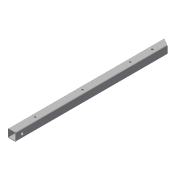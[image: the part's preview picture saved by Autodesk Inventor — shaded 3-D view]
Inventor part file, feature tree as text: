
AUTODESK INVENTOR PART (.ipt)
format: ipt  version: 2016 (Build 200138000, 138)  size: 203,264 bytes
history: native  units: in
note: dims shown in document units (in); Inventor stores cm internally (conversion verified against a paired STEP export)
features: sketch x6, hole x4, extrude x1
ambient origin geometry x8: Origin, YZ Plane, XZ Plane, XY Plane, X Axis, Y Axis, Z Axis, Center Point
bodies: Solid1 (feature_tree)
feature tree (11):
  hole  "centerHole_cutOff"  [1 undecoded]
  hole  "collarHole"  [1 undecoded]
  hole  "armAttach"  [1 undecoded]
  hole  "ropeAttach"  [1 undecoded]
  extrude  "angledEnd"  Depth=1.0in
  sketch  "Sketch1"  dims[d0=1.0in d2=1.0in]
  sketch  "Sketch6"  dims[d3=0.125in d4=0.065in]
  sketch  "Sketch8"  dims[d5=20.4843in d6=0.0in d27=0.7874in]
  sketch  "Sketch11"  dims[d28=0.315in d29=0.75in d30=0.375in d31=0.25in d32=0.5635in d33=1.0in d34=0.8108in d43=0.125in]
  sketch  "Sketch12"  dims[d45=1.1811in d47=5.9055in d48=0.3937in d50=1.0in]
  sketch  "Sketch13"  dims[d52=0.2165in d53=0.75in d54=0.375in d55=0.25in d56=0.5635in d57=1.0in d58=0.8108in d83=0.7874in d84=0.25in d85=0.75in d86=0.375in d87=0.25in d88=0.5635in d89=1.0in d90=0.8108in d91=2.2441in d92=0.2598in d93=0.75in d94=0.375in d95=0.25in d96=0.5635in d97=1.0in d98=0.8108in d99=5.0in d100=0.578in d101=2.0in d102=30.0deg d103=2.0in d104=0.0in d76=1.0in d77=1.0in]
note: 4 required parameter values undecoded (feature->parameter linkage not recoverable at this tier; creation-order binding heuristic only, values carry confidence <= 0.55)
